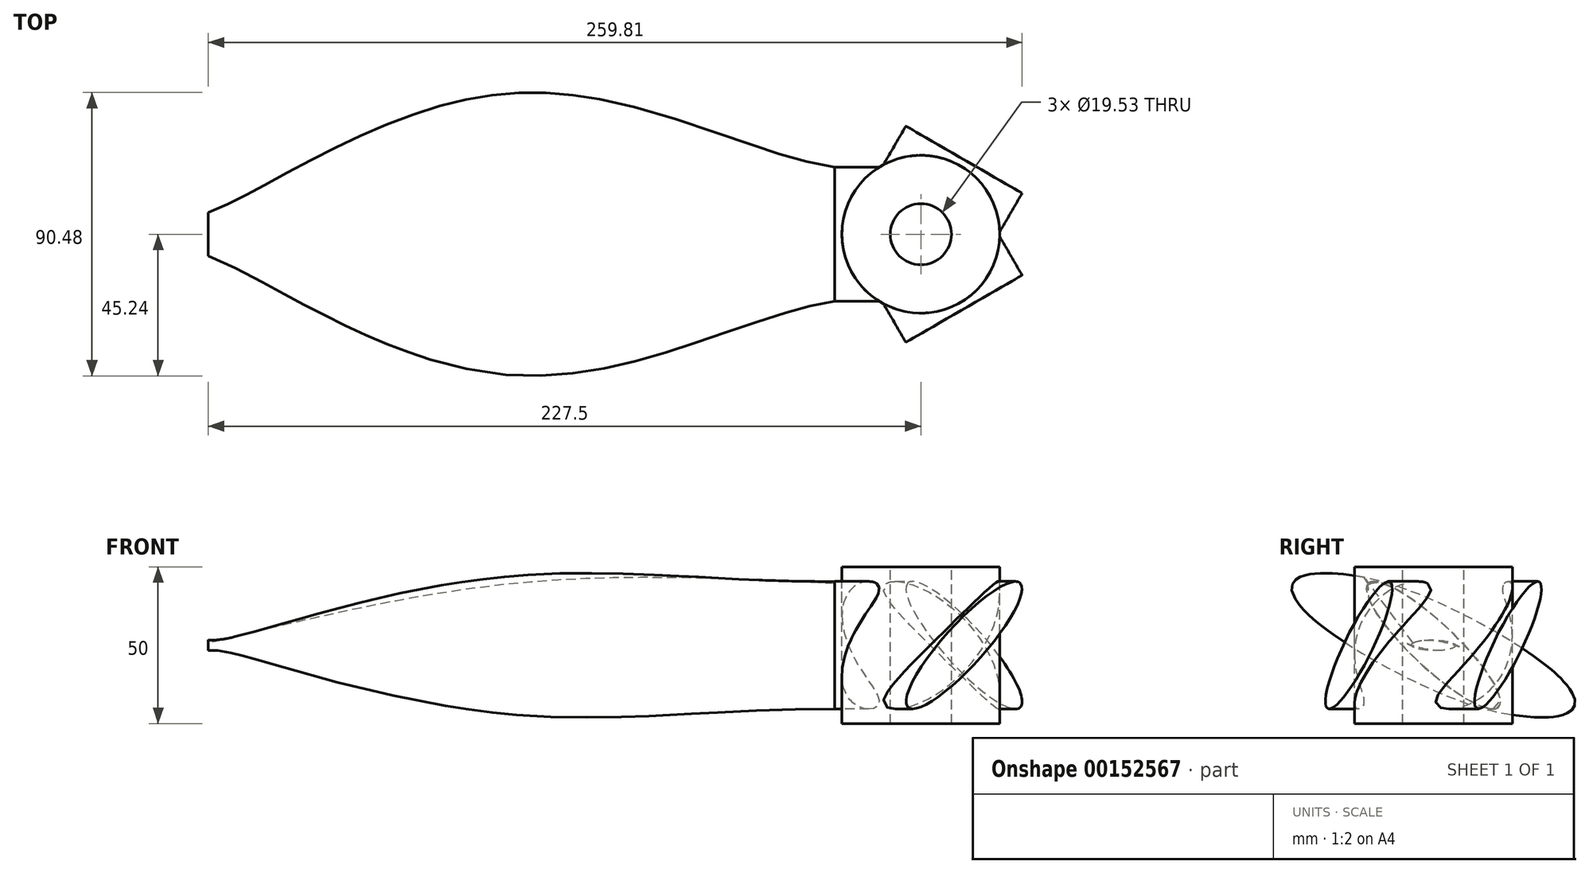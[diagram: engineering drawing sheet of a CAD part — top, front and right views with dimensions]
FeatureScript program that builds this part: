
annotation { "Feature Type Name" : "Feature", "Feature Type Description" : "" }
export const myFeature = defineFeature(function(context is Context, id is Id, definition is map)
    precondition{}
    {
        {
            var Q0;
            Q0=qCreatedBy(makeId("Right.planeOp"),FACE);
            var sketch = newSketch(context, id + "F0", { "sketchPlane" : qUnion([Q0])});
            skLineSegment(sketch, "E0.bottom", {"start": v(-213.06, 65.62) * mm, "end": v(-238.25, 65.62) * mm});
            skLineSegment(sketch, "E0.top", {"start": v(-213.06, 15.62) * mm, "end": v(-238.25, 15.62) * mm});
            skLineSegment(sketch, "E0.left", {"start": v(-213.06, 65.62) * mm, "end": v(-213.06, 15.62) * mm});
            skLineSegment(sketch, "E0.right", {"start": v(-238.25, 65.62) * mm, "end": v(-238.25, 15.62) * mm});
            skSolve(sketch);
        }
        {
            var Q0;
            Q0 = qSketchRegion(id + "F0", true);
            var Q1;
            Q1=sQuery(id+"F0.wireOp",EDGE,"E0.left");
            revolve(context, id + "F1", {"entities" : qUnion([Q0]), "axis" : qUnion([Q1]), "revolveType" : RevolveType.FULL});
        }
        {
            var Q0;
            Q0=makeQuery(id+"F1.opRevolve","SWEPT_FACE",FACE,{"disambiguationData":[OSD([sQuery(id+"F0.wireOp",EDGE,"E0.bottom")])]});
            var sketch = newSketch(context, id + "F2", { "sketchPlane" : qUnion([Q0])});
            skCircle(sketch, "E1", {"center": v(0, -213.06) * mm, "radius": 9.76 * mm});
            skSolve(sketch);
        }
        {
            var Q0;
            Q0=makeQuery(id+"F0.imprint","IMPRINT",FACE,{"disambiguationData":[TD([[makeQuery(id+"F0.imprint","IMPRINT",EDGE,{"derivedFrom":sQuery(id+"F0.wireOp",EDGE,"E0.bottom")}),1.0]])]});
            var sketch = newSketch(context, id + "F3", { "sketchPlane" : qUnion([Q0])});
            skLineSegment(sketch, "E2.0", {"start": v(-213.06, 65.62) * mm, "end": v(-213.06, 15.62) * mm});
            skLineSegment(sketch, "E3.0", {"start": v(-238.25, 65.62) * mm, "end": v(-187.87, 65.62) * mm});
            skLineSegment(sketch, "E4.0", {"start": v(-238.25, 15.62) * mm, "end": v(-187.87, 15.62) * mm});
            skEllipse(sketch, "E5", {"center": v(-213.06, 40.62) * mm, "majorRadius": 28.71 * mm, "minorRadius": 7.07 * mm, "majorAxis": v(-0.73, 0.69)});
            skSolve(sketch);
        }
        {
            var Q0;
            Q0 = qSketchRegion(id + "F3", true);
            extrude(context, id + "F4", {"entities" : qUnion([Q0]), "operationType" : NewBodyOperationType.ADD, "oppositeDirection" : true, "depth" : 27.5 * mm});
        }
        {
            var Q0;
            Q0=makeQuery(id+"F4.opExtrude","CAP_FACE",FACE,{"disambiguationData":[OSD([sQuery(id+"F3.wireOp",EDGE,"E5")])],"isStart":false});
            cPlane(context, id + "F5", {"entities" : qUnion([Q0]), "cplaneType" : CPlaneType.OFFSET, "offset" : 200 * mm, "width" : 150 * mm, "height" : 150 * mm});
        }
        {
            var Q0;
            Q0 = qSketchRegion(id + "F2", true);
            var Q1;
            Q1=makeQuery(id+"F1.opRevolve","SWEPT_FACE",FACE,{"disambiguationData":[OSD([sQuery(id+"F0.wireOp",EDGE,"E0.top")])]});
            extrude(context, id + "F6", {"entities" : qUnion([Q0]), "operationType" : NewBodyOperationType.REMOVE, "endBound" : BoundingType.UP_TO_SURFACE, "oppositeDirection" : true, "endBoundEntityFace" : qUnion([Q1]), "depth" : 25 * mm});
        }
        {
            var Q0;
            Q0=makeQuery(id+"F1.opRevolve","SWEPT_BODY",BODY,{"disambiguationData":[OSD([sQuery(id+"F0.wireOp",EDGE,"E0.bottom"),sQuery(id+"F0.wireOp",EDGE,"E0.top"),sQuery(id+"F0.wireOp",EDGE,"E0.left"),sQuery(id+"F0.wireOp",EDGE,"E0.right")])]});
            var Q1;
            Q1=sQuery(id+"F0.wireOp",EDGE,"E0.left");
            circularPattern(context, id + "F7", {"entities" : qUnion([Q0]), "axis" : qUnion([Q1]), "angle" : 360 * degree, "instanceCount" : 3, "equalSpace" : true});
        }
        {
            var Q0;
            Q0=qCreatedBy(id+"F5.planeOp",FACE);
            cPlane(context, id + "F8", {"entities" : qUnion([Q0]), "cplaneType" : CPlaneType.OFFSET, "offset" : 100 * mm, "oppositeDirection" : true, "width" : 150 * mm, "height" : 150 * mm});
        }
        {
            var Q0;
            Q0=qCreatedBy(id+"F8.planeOp",FACE);
            var sketch = newSketch(context, id + "F9", { "sketchPlane" : qUnion([Q0])});
            skEllipse(sketch, "E6.0", {"center": v(213.06, 40.62) * mm, "majorRadius": 48.94 * mm, "minorRadius": 12.05 * mm, "majorAxis": v(0.92, 0.4)});
            skSolve(sketch);
        }
        {
            var Q0;
            Q0=qCreatedBy(id+"F5.planeOp",FACE);
            var sketch = newSketch(context, id + "F10", { "sketchPlane" : qUnion([Q0])});
            skEllipse(sketch, "E7.0", {"center": v(213.06, 40.62) * mm, "majorRadius": 6.95 * mm, "minorRadius": 1.71 * mm, "majorAxis": v(1, 0.02)});
            skSolve(sketch);
        }
        {
            var Q0;
            Q0=makeQuery(id+"F4.opExtrude","CAP_FACE",FACE,{"disambiguationData":[OSD([sQuery(id+"F3.wireOp",EDGE,"E5")])],"isStart":false});
            var Q1;
            Q1=makeQuery(id+"F9.imprint","IMPRINT",FACE,{"disambiguationData":[TD([[makeQuery(id+"F9.imprint","IMPRINT",EDGE,{"derivedFrom":sQuery(id+"F9.wireOp",EDGE,"E6.0")}),1.0]])]});
            var Q2;
            Q2=makeQuery(id+"F10.imprint","IMPRINT",FACE,{"disambiguationData":[TD([[makeQuery(id+"F10.imprint","IMPRINT",EDGE,{"derivedFrom":sQuery(id+"F10.wireOp",EDGE,"E7.0")}),1.0]])]});
            loft(context, id + "F11", {"sheetProfilesArray" : [{ "sheetProfileEntities" : qUnion([Q0]) }, { "sheetProfileEntities" : qUnion([Q1]) }, { "sheetProfileEntities" : qUnion([Q2]) }]});
        }
    });
